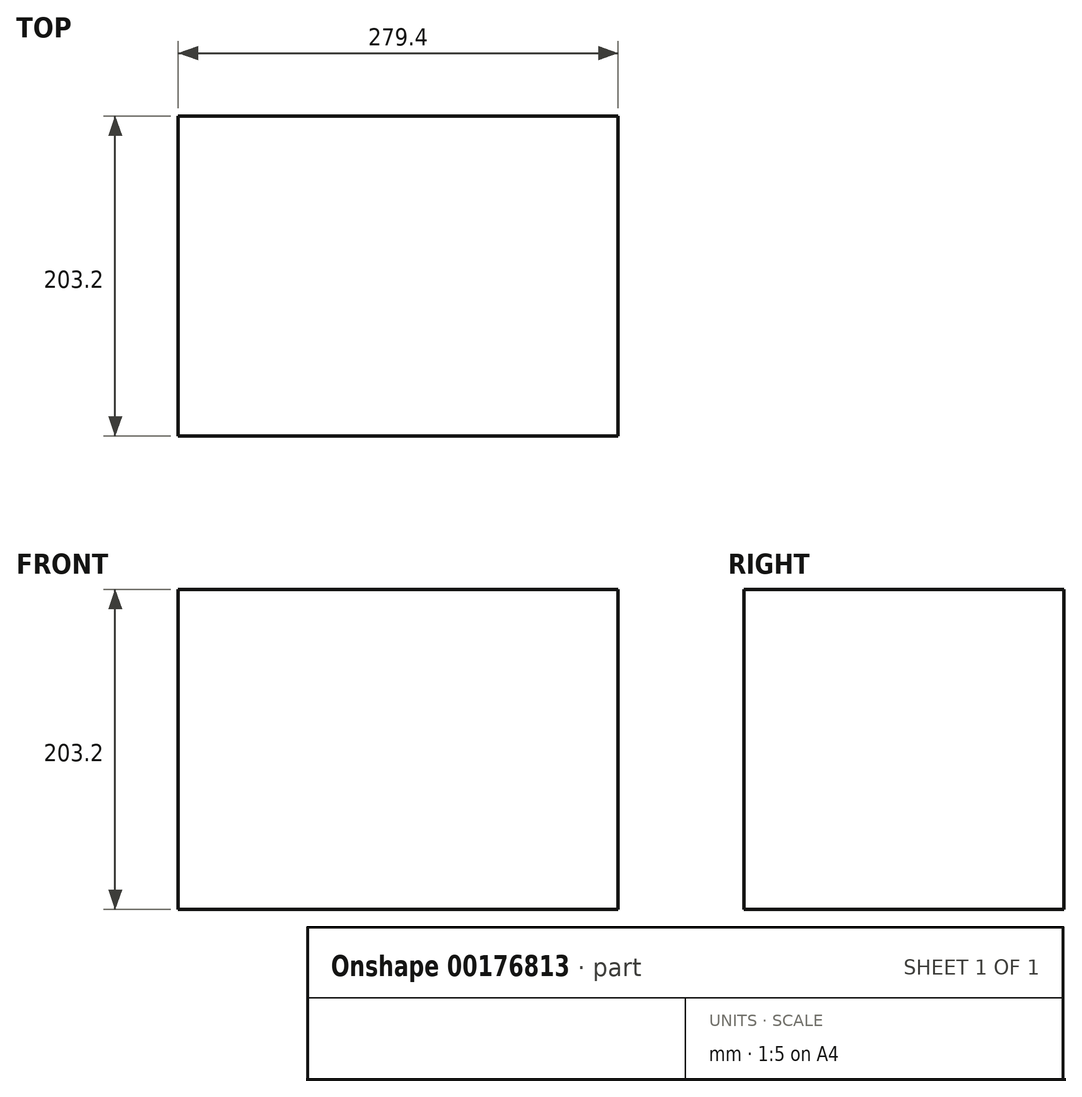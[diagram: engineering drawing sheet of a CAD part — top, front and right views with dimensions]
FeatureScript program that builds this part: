
annotation { "Feature Type Name" : "Feature", "Feature Type Description" : "" }
export const myFeature = defineFeature(function(context is Context, id is Id, definition is map)
    precondition{}
    {
        {
            var Q0;
            Q0=qCreatedBy(makeId("Top.planeOp"),FACE);
            var sketch = newSketch(context, id + "F0", { "sketchPlane" : qUnion([Q0])});
            skLineSegment(sketch, "E0.bottom", {"start": v(139.7, 101.6) * mm, "end": v(-139.7, 101.6) * mm});
            skLineSegment(sketch, "E0.top", {"start": v(139.7, -101.6) * mm, "end": v(-139.7, -101.6) * mm});
            skLineSegment(sketch, "E0.left", {"start": v(139.7, 101.6) * mm, "end": v(139.7, -101.6) * mm});
            skLineSegment(sketch, "E0.right", {"start": v(-139.7, 101.6) * mm, "end": v(-139.7, -101.6) * mm});
            skPoint(sketch, "E0.middle", {"position": v(0, 0) * mm});
            skSolve(sketch);
        }
        {
            var Q0;
            Q0 = qSketchRegion(id + "F0", true);
            extrude(context, id + "F1", {"entities" : qUnion([Q0]), "depth" : 203.2 * mm});
        }
    });
